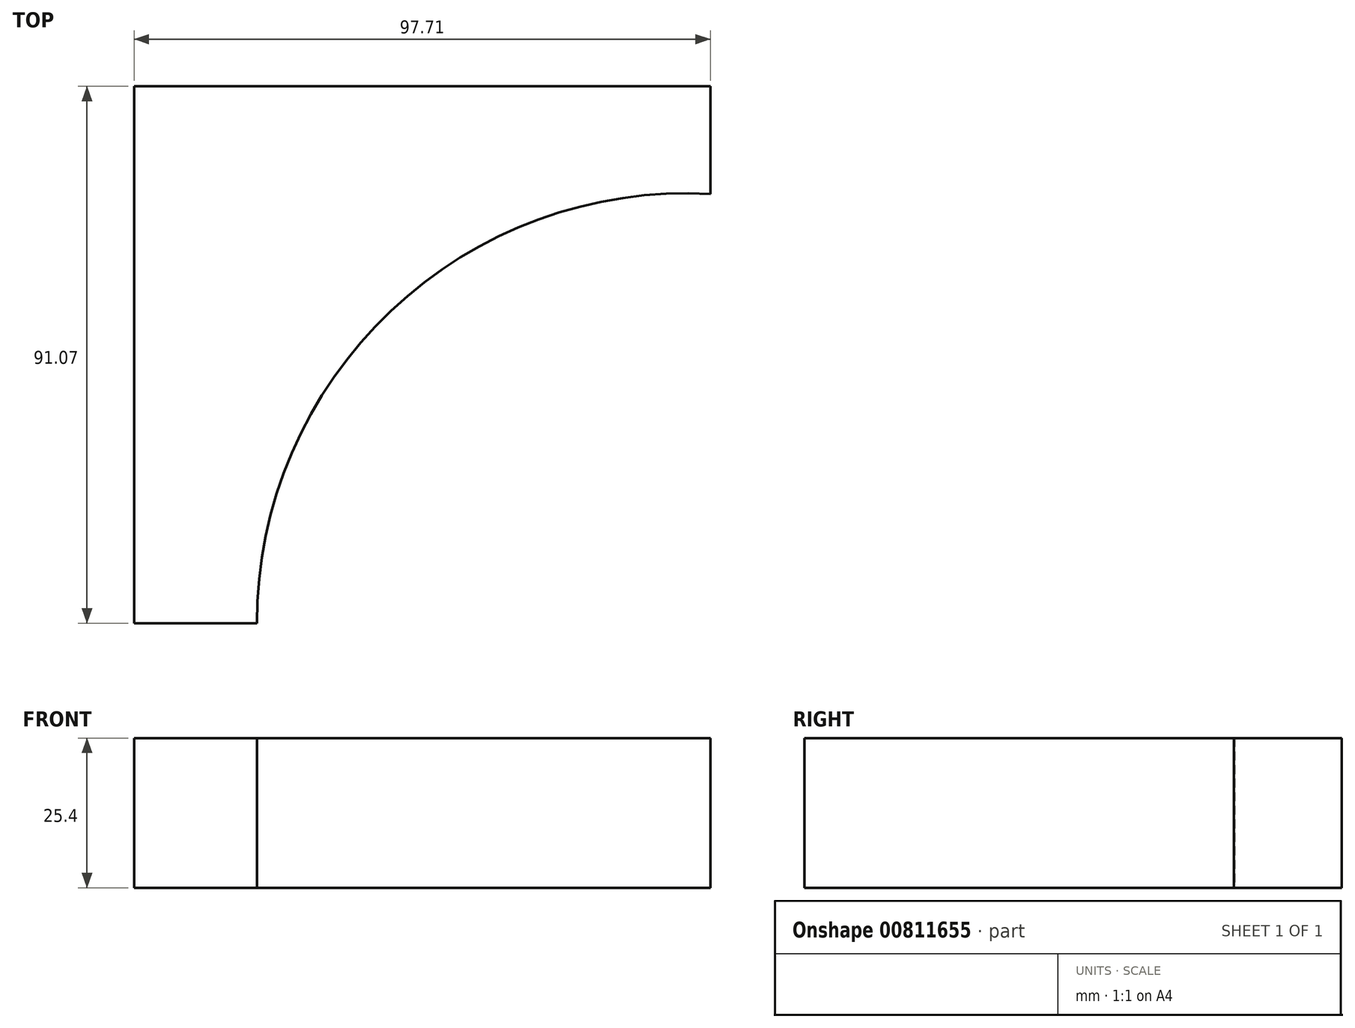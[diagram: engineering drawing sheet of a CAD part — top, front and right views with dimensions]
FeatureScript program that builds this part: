
annotation { "Feature Type Name" : "Feature", "Feature Type Description" : "" }
export const myFeature = defineFeature(function(context is Context, id is Id, definition is map)
    precondition{}
    {
        {
            var Q0;
            Q0=qCreatedBy(makeId("Top.planeOp"),FACE);
            var sketch = newSketch(context, id + "F0", { "sketchPlane" : qUnion([Q0])});
            skLineSegment(sketch, "E0", {"start": v(-45.26, 34.75) * mm, "end": v(52.45, 34.75) * mm});
            skLineSegment(sketch, "E1", {"start": v(52.45, 34.75) * mm, "end": v(52.45, 16.5) * mm});
            skLineSegment(sketch, "E2", {"start": v(-45.26, 34.75) * mm, "end": v(-45.26, -56.32) * mm});
            skLineSegment(sketch, "E3", {"start": v(-45.26, -56.32) * mm, "end": v(-24.43, -56.32) * mm});
            skArc(sketch, "E4", {"start": v(52.45, 16.5) * mm, "mid": v(-1.7, -3.33) * mm, "end": v(-24.43, -56.32) * mm});
            skSolve(sketch);
        }
        {
            var Q0;
            Q0=makeQuery(id+"F0.imprint","IMPRINT",FACE,{"disambiguationData":[TD([[makeQuery(id+"F0.imprint","IMPRINT",EDGE,{"derivedFrom":sQuery(id+"F0.wireOp",EDGE,"E0")}),-1.0]])]});
            extrude(context, id + "F1", {"entities" : qUnion([Q0]), "depth" : 25.4 * mm, "offsetDistance" : 25.4 * mm});
        }
    });
